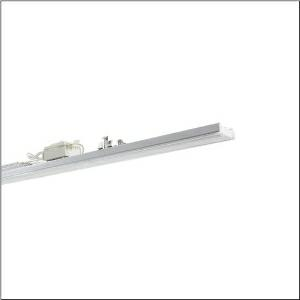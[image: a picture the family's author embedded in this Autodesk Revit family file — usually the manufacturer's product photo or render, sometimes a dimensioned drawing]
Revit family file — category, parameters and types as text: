
# Revit family: licross_r__21_recessed_mo_52tl12dn6axg_fe94
name_source: partatom
category: Lighting Fixtures
units: mm (PartAtom-declared; Revit-internal decimal feet)

## family parameters
Cut with Voids When Loaded = No
Host = Face
Light Source = No
Part Type = Normal
Room Calculation Point = No
Round Connector Dimension = Use Diameter
Shared = No

## types (1)
- --- (1 x LED, 10000 lm, 58 W, 6500K)
    Apparent Load = 58 VA
    CIE Flux Codes = 72 92 99 100 100
    Color Rendering = 80
    Color Temperature = 6500K
    Default Elevation = 1800 mm
    Description = Licross® 21 Recessed MO, luminaire insert, of sheet steel, galvanised, coil coated, white, length: 1.500mm, width: 66mm, height: 67mm, LED rated luminous flux: 10.000lm, light colour: 865, control gear: DALI 2, with plug, 5-pole, with phase selection, mains connection: 220..240V, AC, 50/60Hz, rated input power: 58W, halogen-free wiring, primary optical cover: cover, of PMMA, light emission: direct distribution, primary light characteristic: symmetric, protection rating (complete): IP40, insulation class (complete): insulation class I (protective earthing), certification: CE, ENEC, VDE, UKCA, protection symbol: D if used in an environment without relevant dust loads with corresponding accessories, impact resistance: IK06, permissible ambient temperature for indoor applications: -25..+35°C, corresponds to IFS (International Featured Standards) requirements for safety and quality in the food industry, reducing of maximum allowable ambient temperature of 5°C with ceiling mounting, LABS conformity tested according to VDMA 24364:2018-05, packaging unit: 1 piece
    Height = 58 mm
    Lamp = 1 x LED
    Lamp Light Flux = 10000 lm
    Lamp Power = 58 W
    Lamp count = 1
    Length = 1500 mm
    Luminous efficacy = 172 lm/W
    Manufacturer = Siteco
    ModVariant = No
    Model = 52TL12DN6AXG
    Mounting Place = Ceiling
    Mounting Type = Pendant
    Number of Poles = 1
    OnlyDefault = Yes
    Power Factor = 1
    Product Name = Licross® 21 Recessed MO
    Product group = luminaire insert
    ProductGroupID = 902
    Protection Class = Protection class I
    Protection Degree = IP 40
    RLX_Detail_Level = 1
    RLX_Emergency_Light_Flux = 0 lm
    RLX_Emergency_Type = 0
    RLX_Emergency_Type_DB = No
    RlxData = <blob elided: 24553 chars, md5=20cda7fc>
    Socket = socket
    Standby Power = 0 W
    System Light Flux = 10000 lm
    System Power = 58 W
    Type Comments = factory setting: luminous flux: 100 % | dim-lin: 254 | 390 mA
    Type Image = l_1296930.jpg
    URL = http://relux.com
    VarID = @adj_089530
    Voltage = 0 V
    Weight = 0.00 kg
    Width = 66 mm

## geometry (parser evidence)
native form markers: Blend x4, Sweep x12
no freeform markers — native parametric forms only
